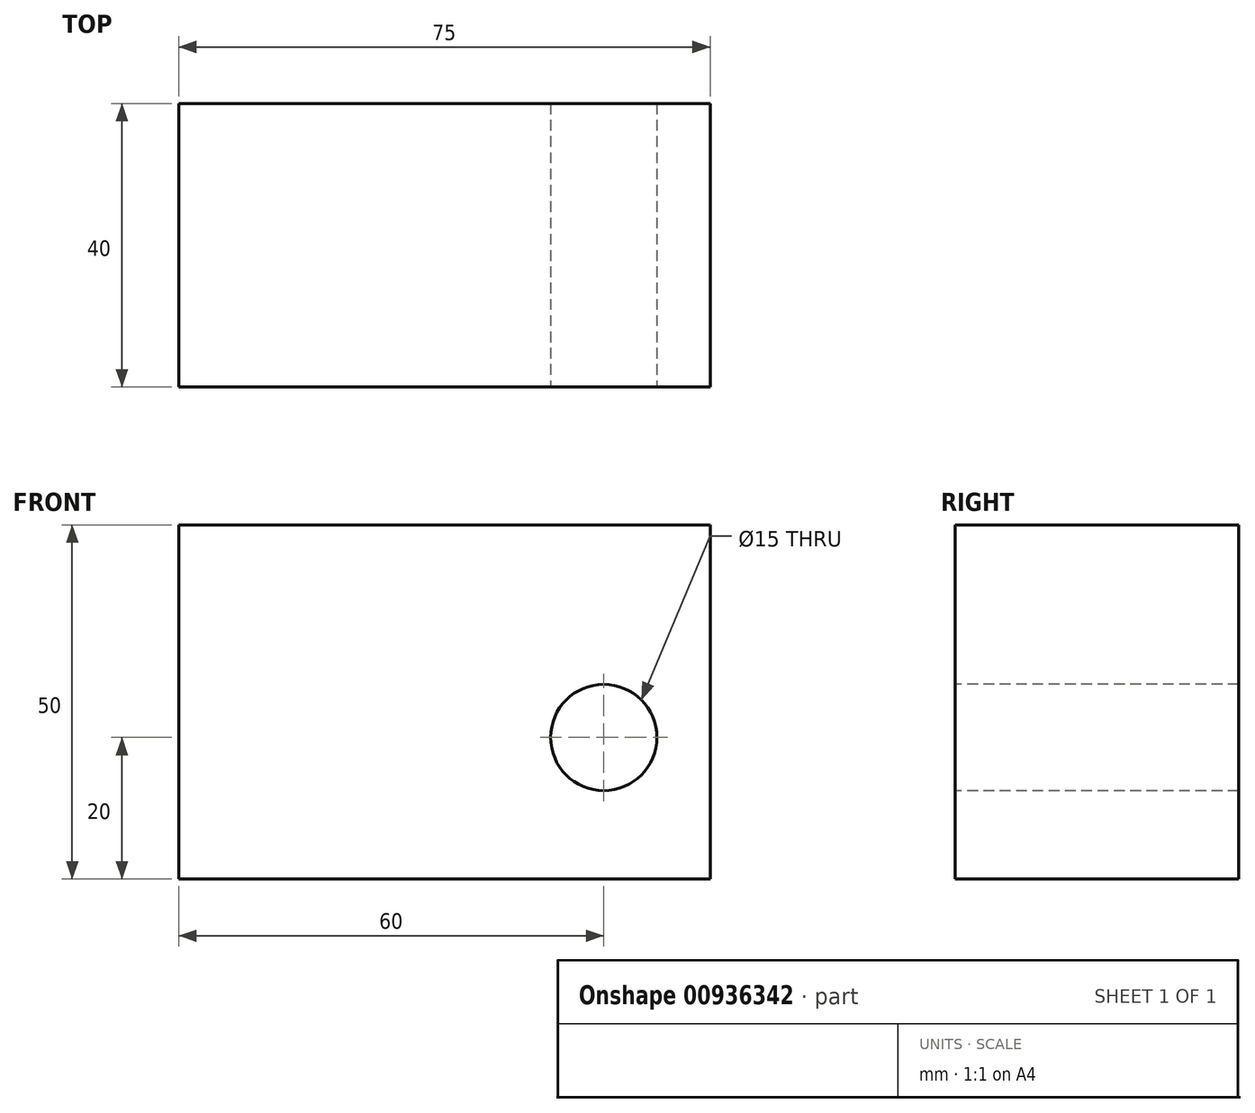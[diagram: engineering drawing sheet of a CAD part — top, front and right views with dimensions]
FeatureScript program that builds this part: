
annotation { "Feature Type Name" : "Feature", "Feature Type Description" : "" }
export const myFeature = defineFeature(function(context is Context, id is Id, definition is map)
    precondition{}
    {
        {
            var Q0;
            Q0=qCreatedBy(makeId("Front.planeOp"),FACE);
            var sketch = newSketch(context, id + "F0", { "sketchPlane" : qUnion([Q0])});
            skLineSegment(sketch, "E0", {"start": v(-60, 30) * mm, "end": v(15, 30) * mm});
            skLineSegment(sketch, "E1", {"start": v(15, 30) * mm, "end": v(15, -20) * mm});
            skLineSegment(sketch, "E2", {"start": v(15, -20) * mm, "end": v(-60, -20) * mm});
            skLineSegment(sketch, "E3", {"start": v(-60, -20) * mm, "end": v(-60, 30) * mm});
            skSolve(sketch);
        }
        {
            var Q0;
            Q0=makeQuery(id+"F0.imprint","IMPRINT",FACE,{"disambiguationData":[TD([[makeQuery(id+"F0.imprint","IMPRINT",EDGE,{"derivedFrom":sQuery(id+"F0.wireOp",EDGE,"E0")}),-1.0]])]});
            extrude(context, id + "F1", {"entities" : qUnion([Q0]), "depth" : 40 * mm, "offsetDistance" : 25 * mm, "symmetric" : true});
        }
        {
            var Q0;
            Q0=makeQuery(id+"F1.opExtrude","CAP_FACE",FACE,{"disambiguationData":[OSD([sQuery(id+"F0.wireOp",EDGE,"E0"),sQuery(id+"F0.wireOp",EDGE,"E1"),sQuery(id+"F0.wireOp",EDGE,"E2"),sQuery(id+"F0.wireOp",EDGE,"E3")])],"isStart":false});
            var sketch = newSketch(context, id + "F2", { "sketchPlane" : qUnion([Q0])});
            skCircle(sketch, "E4", {"center": v(0, 0) * mm, "radius": 7.5 * mm});
            skSolve(sketch);
        }
        {
            var Q0;
            Q0 = qSketchRegion(id + "F2", true);
            var Q1;
            Q1=makeQuery(id+"F1.opExtrude","CAP_FACE",FACE,{"disambiguationData":[OSD([sQuery(id+"F0.wireOp",EDGE,"E0"),sQuery(id+"F0.wireOp",EDGE,"E1"),sQuery(id+"F0.wireOp",EDGE,"E2"),sQuery(id+"F0.wireOp",EDGE,"E3")])],"isStart":true});
            extrude(context, id + "F3", {"entities" : qUnion([Q0]), "operationType" : NewBodyOperationType.REMOVE, "endBound" : BoundingType.UP_TO_SURFACE, "oppositeDirection" : true, "depth" : 25 * mm, "endBoundEntityFace" : qUnion([Q1]), "offsetDistance" : 25 * mm});
        }
    });
